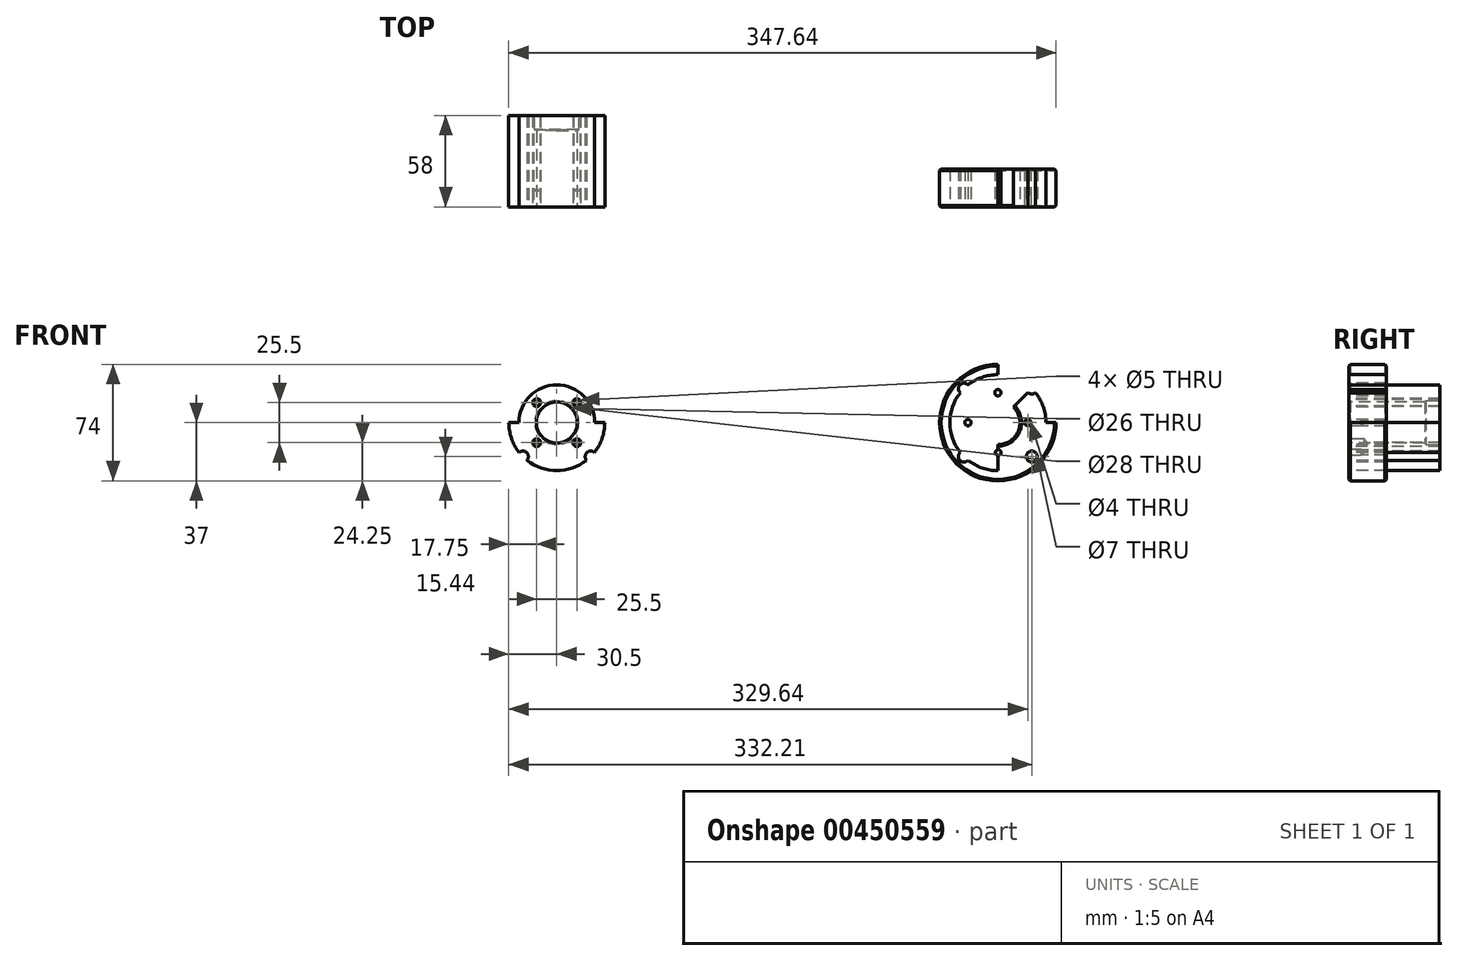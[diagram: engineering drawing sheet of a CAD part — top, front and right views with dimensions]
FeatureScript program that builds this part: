
annotation { "Feature Type Name" : "Feature", "Feature Type Description" : "" }
export const myFeature = defineFeature(function(context is Context, id is Id, definition is map)
    precondition{}
    {
        {
            var Q0;
            Q0=qCreatedBy(makeId("Front.planeOp"),FACE);
            var sketch = newSketch(context, id + "F0", { "sketchPlane" : qUnion([Q0])});
            skLineSegment(sketch, "E0", {"start": v(-17.52, 38.45) * mm, "end": v(-17.52, 26.45) * mm});
            skLineSegment(sketch, "E1", {"start": v(-17.52, -21.55) * mm, "end": v(-17.52, -33.55) * mm});
            skCircle(sketch, "E2", {"center": v(103.48, 2.45) * mm, "radius": 19 * mm});
            skLineSegment(sketch, "E3", {"start": v(103.48, 24.95) * mm, "end": v(103.48, 17.95) * mm});
            skLineSegment(sketch, "E4", {"start": v(103.48, -13.05) * mm, "end": v(103.48, -20.05) * mm});
            skLineSegment(sketch, "E5", {"start": v(-16.52, -34.55) * mm, "end": v(5.48, -34.55) * mm});
            skLineSegment(sketch, "E6", {"start": v(-16.52, 39.45) * mm, "end": v(5.48, 39.45) * mm});
            skLineSegment(sketch, "E7", {"start": v(6.48, -33.55) * mm, "end": v(6.48, -12.55) * mm});
            skLineSegment(sketch, "E8", {"start": v(5.48, -11.55) * mm, "end": v(-26.52, -11.55) * mm});
            skLineSegment(sketch, "E9", {"start": v(-26.52, -10.55) * mm, "end": v(-75.52, -10.55) * mm});
            skLineSegment(sketch, "E10", {"start": v(-74.52, -21.55) * mm, "end": v(-17.52, -21.55) * mm});
            skLineSegment(sketch, "E11", {"start": v(-74.52, 26.45) * mm, "end": v(-17.52, 26.45) * mm});
            skLineSegment(sketch, "E12", {"start": v(-75.52, 25.45) * mm, "end": v(-75.52, -20.55) * mm});
            skLineSegment(sketch, "E13", {"start": v(-5.25, -16.55) * mm, "end": v(6.48, -16.55) * mm});
            skLineSegment(sketch, "E14", {"start": v(6.48, -14.55) * mm, "end": v(-1.52, -14.55) * mm});
            skLineSegment(sketch, "E15", {"start": v(6.48, -18.55) * mm, "end": v(-1.52, -18.55) * mm});
            skLineSegment(sketch, "E16", {"start": v(6.48, -18.17) * mm, "end": v(-4.32, -18.17) * mm});
            skLineSegment(sketch, "E17", {"start": v(6.48, -14.92) * mm, "end": v(-4.32, -14.92) * mm});
            skLineSegment(sketch, "E18", {"start": v(-1.52, -18.55) * mm, "end": v(-1.52, -14.55) * mm});
            skLineSegment(sketch, "E19", {"start": v(-5.25, -16.55) * mm, "end": v(-4.32, -14.92) * mm});
            skLineSegment(sketch, "E20", {"start": v(-4.32, -18.17) * mm, "end": v(-4.32, -14.92) * mm});
            skLineSegment(sketch, "E21", {"start": v(-1.52, -14.55) * mm, "end": v(-2.22, -14.92) * mm});
            skLineSegment(sketch, "E22", {"start": v(-1.52, -18.55) * mm, "end": v(-2.22, -18.17) * mm});
            skLineSegment(sketch, "E23", {"start": v(-5.25, -16.55) * mm, "end": v(-4.32, -18.17) * mm});
            skLineSegment(sketch, "E24", {"start": v(-26.52, -11.55) * mm, "end": v(-26.52, 16.45) * mm});
            skLineSegment(sketch, "E25", {"start": v(5.48, 16.45) * mm, "end": v(-26.52, 16.45) * mm});
            skLineSegment(sketch, "E26", {"start": v(-26.52, 15.45) * mm, "end": v(-75.52, 15.45) * mm});
            skLineSegment(sketch, "E27", {"start": v(125.48, 2.45) * mm, "end": v(119.48, 2.45) * mm});
            skCircle(sketch, "E28", {"center": v(122.48, 2.45) * mm, "radius": 2 * mm});
            skCircle(sketch, "E29", {"center": v(122.48, 2.45) * mm, "radius": 1.62 * mm});
            skLineSegment(sketch, "E30", {"start": v(103.48, 18.45) * mm, "end": v(103.48, 24.45) * mm});
            skCircle(sketch, "E31", {"center": v(103.48, 21.45) * mm, "radius": 2 * mm});
            skCircle(sketch, "E32", {"center": v(103.48, 21.45) * mm, "radius": 1.62 * mm});
            skLineSegment(sketch, "E33", {"start": v(87.48, 2.45) * mm, "end": v(81.48, 2.45) * mm});
            skCircle(sketch, "E34", {"center": v(84.48, 2.45) * mm, "radius": 2 * mm});
            skCircle(sketch, "E35", {"center": v(84.48, 2.45) * mm, "radius": 1.62 * mm});
            skLineSegment(sketch, "E36", {"start": v(103.48, -19.55) * mm, "end": v(103.48, -13.55) * mm});
            skCircle(sketch, "E37", {"center": v(103.48, -16.55) * mm, "radius": 2 * mm});
            skCircle(sketch, "E38", {"center": v(103.48, -16.55) * mm, "radius": 1.62 * mm});
            skCircle(sketch, "E39", {"center": v(103.48, 2.45) * mm, "radius": 14 * mm});
            skLineSegment(sketch, "E40", {"start": v(115.98, 2.45) * mm, "end": v(128.98, 2.45) * mm});
            skCircle(sketch, "E41", {"center": v(103.48, 2.45) * mm, "radius": 13 * mm});
            skCircle(sketch, "E42", {"center": v(-176.66, 2.45) * mm, "radius": 24 * mm});
            skCircle(sketch, "E43", {"center": v(-176.66, 2.45) * mm, "radius": 13 * mm});
            skLineSegment(sketch, "E44", {"start": v(-81.8, 2.45) * mm, "end": v(11.92, 2.45) * mm});
            skLineSegment(sketch, "E45", {"start": v(-163.91, 11.45) * mm, "end": v(-163.91, 18.95) * mm});
            skCircle(sketch, "E46", {"center": v(-163.91, 15.2) * mm, "radius": 2.07 * mm});
            skCircle(sketch, "E47", {"center": v(-163.91, 15.2) * mm, "radius": 2.5 * mm});
            skLineSegment(sketch, "E48", {"start": v(-160.16, 15.2) * mm, "end": v(-167.66, 15.2) * mm});
            skLineSegment(sketch, "E49", {"start": v(-163.91, -14.05) * mm, "end": v(-163.91, -6.55) * mm});
            skCircle(sketch, "E50", {"center": v(-163.91, -10.3) * mm, "radius": 2.07 * mm});
            skCircle(sketch, "E51", {"center": v(-163.91, -10.3) * mm, "radius": 2.5 * mm});
            skLineSegment(sketch, "E52", {"start": v(-160.16, -10.3) * mm, "end": v(-167.66, -10.3) * mm});
            skLineSegment(sketch, "E53", {"start": v(-189.41, -14.05) * mm, "end": v(-189.41, -6.55) * mm});
            skCircle(sketch, "E54", {"center": v(-189.41, -10.3) * mm, "radius": 2.07 * mm});
            skCircle(sketch, "E55", {"center": v(-189.41, -10.3) * mm, "radius": 2.5 * mm});
            skLineSegment(sketch, "E56", {"start": v(-185.66, -10.3) * mm, "end": v(-193.16, -10.3) * mm});
            skLineSegment(sketch, "E57", {"start": v(-189.41, 11.45) * mm, "end": v(-189.41, 18.95) * mm});
            skCircle(sketch, "E58", {"center": v(-189.41, 15.2) * mm, "radius": 2.07 * mm});
            skCircle(sketch, "E59", {"center": v(-189.41, 15.2) * mm, "radius": 2.5 * mm});
            skLineSegment(sketch, "E60", {"start": v(-185.66, 15.2) * mm, "end": v(-193.16, 15.2) * mm});
            skLineSegment(sketch, "E61", {"start": v(103.48, 47.95) * mm, "end": v(103.48, -43.05) * mm});
            skLineSegment(sketch, "E62", {"start": v(57.98, 2.45) * mm, "end": v(148.98, 2.45) * mm});
            skLineSegment(sketch, "E63", {"start": v(-176.66, 47.95) * mm, "end": v(-176.66, -43.05) * mm});
            skLineSegment(sketch, "E64", {"start": v(-222.16, 2.45) * mm, "end": v(-131.16, 2.45) * mm});
            skLineSegment(sketch, "E65", {"start": v(10.78, -9.05) * mm, "end": v(12.23, -11.55) * mm});
            skLineSegment(sketch, "E66", {"start": v(12.23, -11.55) * mm, "end": v(15.4, -6.05) * mm});
            skLineSegment(sketch, "E67", {"start": v(15.4, -6.05) * mm, "end": v(21.78, -6.05) * mm});
            skLineSegment(sketch, "E68", {"start": v(10.78, -9.05) * mm, "end": v(13.67, -9.05) * mm});
            skLineSegment(sketch, "E69", {"start": v(6.48, -33.55) * mm, "end": v(5.48, -34.55) * mm});
            skLineSegment(sketch, "E70", {"start": v(6.48, 38.45) * mm, "end": v(5.48, 39.45) * mm});
            skCircle(sketch, "E71", {"center": v(103.48, 2.45) * mm, "radius": 37 * mm});
            skCircle(sketch, "E72", {"center": v(103.48, 2.45) * mm, "radius": 30.5 * mm});
            skCircle(sketch, "E73", {"center": v(81.92, 24.02) * mm, "radius": 3.5 * mm});
            skCircle(sketch, "E74", {"center": v(81.92, -19.11) * mm, "radius": 3.5 * mm});
            skCircle(sketch, "E75", {"center": v(125.05, 24.02) * mm, "radius": 3.5 * mm});
            skCircle(sketch, "E76", {"center": v(125.05, -19.11) * mm, "radius": 3.5 * mm});
            skCircle(sketch, "E77", {"center": v(-176.66, 2.45) * mm, "radius": 37 * mm});
            skCircle(sketch, "E78", {"center": v(-198.23, 24.02) * mm, "radius": 3.5 * mm});
            skCircle(sketch, "E79", {"center": v(-198.23, -19.11) * mm, "radius": 3.5 * mm});
            skCircle(sketch, "E80", {"center": v(-155.1, 24.02) * mm, "radius": 3.5 * mm});
            skCircle(sketch, "E81", {"center": v(-155.1, -19.11) * mm, "radius": 3.5 * mm});
            skCircle(sketch, "E82", {"center": v(-176.66, 2.45) * mm, "radius": 30.5 * mm});
            skLineSegment(sketch, "E83", {"start": v(128.27, 27.24) * mm, "end": v(121.83, 20.8) * mm});
            skLineSegment(sketch, "E84", {"start": v(78.7, 27.24) * mm, "end": v(85.13, 20.8) * mm});
            skLineSegment(sketch, "E85", {"start": v(78.7, -22.33) * mm, "end": v(85.13, -15.9) * mm});
            skLineSegment(sketch, "E86", {"start": v(128.27, -22.33) * mm, "end": v(121.83, -15.9) * mm});
            skLineSegment(sketch, "E87", {"start": v(-151.88, 27.24) * mm, "end": v(-158.31, 20.8) * mm});
            skLineSegment(sketch, "E88", {"start": v(-201.45, 27.24) * mm, "end": v(-195.01, 20.8) * mm});
            skLineSegment(sketch, "E89", {"start": v(-201.45, -22.33) * mm, "end": v(-195.01, -15.9) * mm});
            skLineSegment(sketch, "E90", {"start": v(-151.88, -22.33) * mm, "end": v(-158.31, -15.9) * mm});
            skLineSegment(sketch, "E91", {"start": v(-24.54, 32.95) * mm, "end": v(11.92, 32.95) * mm});
            skLineSegment(sketch, "E92", {"start": v(-17.52, 36.45) * mm, "end": v(6.48, 36.45) * mm});
            skLineSegment(sketch, "E93", {"start": v(-17.52, 29.45) * mm, "end": v(6.48, 29.45) * mm});
            skLineSegment(sketch, "E94", {"start": v(-61.12, 20.49) * mm, "end": v(-75.52, 20.49) * mm});
            skLineSegment(sketch, "E95", {"start": v(-75.52, 18.42) * mm, "end": v(-62.32, 18.42) * mm});
            skLineSegment(sketch, "E96", {"start": v(-75.52, 22.55) * mm, "end": v(-62.32, 22.55) * mm});
            skLineSegment(sketch, "E97", {"start": v(-62.32, 22.55) * mm, "end": v(-62.32, 18.42) * mm});
            skLineSegment(sketch, "E98", {"start": v(-61.12, 20.49) * mm, "end": v(-62.32, 22.55) * mm});
            skLineSegment(sketch, "E99", {"start": v(-61.12, 20.49) * mm, "end": v(-62.32, 18.42) * mm});
            skLineSegment(sketch, "E100", {"start": v(-75.52, 17.99) * mm, "end": v(-65.52, 17.99) * mm});
            skLineSegment(sketch, "E101", {"start": v(-75.52, 22.99) * mm, "end": v(-65.52, 22.99) * mm});
            skLineSegment(sketch, "E102", {"start": v(-65.52, 22.99) * mm, "end": v(-65.52, 17.99) * mm});
            skLineSegment(sketch, "E103", {"start": v(-65.52, 22.99) * mm, "end": v(-64.72, 22.55) * mm});
            skLineSegment(sketch, "E104", {"start": v(-65.52, 17.99) * mm, "end": v(-64.72, 18.42) * mm});
            skLineSegment(sketch, "E105", {"start": v(103.48, 2.45) * mm, "end": v(134.88, 33.85) * mm});
            skLineSegment(sketch, "E106", {"start": v(103.48, 2.45) * mm, "end": v(103.48, -59.07) * mm});
            skLineSegment(sketch, "E107", {"start": v(135.02, 33.7) * mm, "end": v(136.43, 35.12) * mm});
            skLineSegment(sketch, "E108", {"start": v(134.74, 34) * mm, "end": v(136.15, 35.4) * mm});
            skLineSegment(sketch, "E109", {"start": v(136.43, 35.12) * mm, "end": v(136.15, 35.4) * mm});
            skLineSegment(sketch, "E110", {"start": v(134.74, 34) * mm, "end": v(135.02, 33.7) * mm});
            skLineSegment(sketch, "E111", {"start": v(103.68, -59.07) * mm, "end": v(103.68, -61.07) * mm});
            skLineSegment(sketch, "E112", {"start": v(103.28, -59.07) * mm, "end": v(103.28, -61.07) * mm});
            skLineSegment(sketch, "E113", {"start": v(103.68, -61.07) * mm, "end": v(103.28, -61.07) * mm});
            skLineSegment(sketch, "E114", {"start": v(103.28, -59.07) * mm, "end": v(103.68, -59.07) * mm});
            skLineSegment(sketch, "E115", {"start": v(-16.52, -34.55) * mm, "end": v(-17.52, -33.55) * mm});
            skLineSegment(sketch, "E116", {"start": v(-16.52, 39.45) * mm, "end": v(-17.52, 38.45) * mm});
            skLineSegment(sketch, "E117", {"start": v(-74.52, -21.55) * mm, "end": v(-75.52, -20.55) * mm});
            skLineSegment(sketch, "E118", {"start": v(-74.52, 26.45) * mm, "end": v(-75.52, 25.45) * mm});
            skLineSegment(sketch, "E119", {"start": v(6.48, 17.45) * mm, "end": v(5.48, 16.45) * mm});
            skLineSegment(sketch, "E120", {"start": v(6.48, -12.55) * mm, "end": v(5.48, -11.55) * mm});
            skLineSegment(sketch, "E121", {"start": v(6.48, 38.45) * mm, "end": v(6.48, -12.55) * mm});
            skLineSegment(sketch, "E122", {"start": v(5.48, 16.45) * mm, "end": v(5.48, -11.55) * mm});
            skSolve(sketch);
        }
        {
            var Q0;
            {var subQ3=sQuery(id+"F0.wireOp",EDGE,"E105");var subQ9=makeQuery(id+"F0.imprint","IMPRINT",VERTEX,{"disambiguationData":[OD(1.0)],"derivedFrom":subQ3});Q0=makeQuery(id+"F0.imprint","IMPRINT",FACE,{"disambiguationData":[TD([[makeQuery(id+"F0.imprint","IMPRINT",EDGE,{"disambiguationData":[TD([[subQ9,1.0]])],"derivedFrom":subQ3}),-1.0]])]});}
            var Q1;
            {var subQ0=sQuery(id+"F0.wireOp",EDGE,"E62");var subQ1=makeQuery(id+"F0.imprint","IMPRINT",VERTEX,{"disambiguationData":[OD(4.0)],"derivedFrom":subQ0});Q1=makeQuery(id+"F0.imprint","IMPRINT",FACE,{"disambiguationData":[TD([[makeQuery(id+"F0.imprint","IMPRINT",EDGE,{"disambiguationData":[TD([[subQ1,-1.0]])],"derivedFrom":subQ0}),1.0]])]});}
            var Q2;
            {var subQ0=sQuery(id+"F0.wireOp",EDGE,"E61");var subQ1=makeQuery(id+"F0.imprint","IMPRINT",VERTEX,{"disambiguationData":[OD(0.0)],"derivedFrom":subQ0});Q2=makeQuery(id+"F0.imprint","IMPRINT",FACE,{"disambiguationData":[TD([[makeQuery(id+"F0.imprint","IMPRINT",EDGE,{"disambiguationData":[TD([[subQ1,-1.0]])],"derivedFrom":subQ0}),1.0]])]});}
            var Q3;
            {var subQ3=sQuery(id+"F0.wireOp",EDGE,"E105");var subQ7=makeQuery(id+"F0.imprint","IMPRINT",VERTEX,{"disambiguationData":[OD(1.0)],"derivedFrom":subQ3});Q3=makeQuery(id+"F0.imprint","IMPRINT",FACE,{"disambiguationData":[TD([[makeQuery(id+"F0.imprint","IMPRINT",EDGE,{"disambiguationData":[TD([[subQ7,1.0]])],"derivedFrom":subQ3}),1.0]])]});}
            var Q4;
            {var subQ5=sQuery(id+"F0.wireOp",EDGE,"E71");var subQ6=sQuery(id+"F0.wireOp",EDGE,"E61");var subQ7=makeQuery(id+"F0.imprint","INTERSECT",VERTEX,{"derivedFrom":[subQ6,subQ5]});Q4=makeQuery(id+"F0.imprint","IMPRINT",FACE,{"disambiguationData":[TD([[makeQuery(id+"F0.imprint","IMPRINT",EDGE,{"disambiguationData":[TD([[subQ7,-1.0]])],"derivedFrom":subQ6}),-1.0]])]});}
            var Q5;
            {var subQ1=sQuery(id+"F0.wireOp",EDGE,"E61");var subQ8=makeQuery(id+"F0.imprint","IMPRINT",VERTEX,{"disambiguationData":[OD(0.0)],"derivedFrom":subQ1});Q5=makeQuery(id+"F0.imprint","IMPRINT",FACE,{"disambiguationData":[TD([[makeQuery(id+"F0.imprint","IMPRINT",EDGE,{"disambiguationData":[TD([[subQ8,-1.0]])],"derivedFrom":subQ1}),-1.0]])]});}
            var Q6;
            {var subQ3=sQuery(id+"F0.wireOp",EDGE,"E61");var subQ12=makeQuery(id+"F0.imprint","IMPRINT",VERTEX,{"disambiguationData":[OD(2.0)],"derivedFrom":subQ3});Q6=makeQuery(id+"F0.imprint","IMPRINT",FACE,{"disambiguationData":[TD([[makeQuery(id+"F0.imprint","IMPRINT",EDGE,{"disambiguationData":[TD([[subQ12,-1.0]])],"derivedFrom":subQ3}),-1.0]])]});}
            var Q7;
            {var subQ0=sQuery(id+"F0.wireOp",EDGE,"E61");var subQ1=makeQuery(id+"F0.imprint","IMPRINT",VERTEX,{"disambiguationData":[OD(2.0)],"derivedFrom":subQ0});Q7=makeQuery(id+"F0.imprint","IMPRINT",FACE,{"disambiguationData":[TD([[makeQuery(id+"F0.imprint","IMPRINT",EDGE,{"disambiguationData":[TD([[subQ1,-1.0]])],"derivedFrom":subQ0}),1.0]])]});}
            var Q8;
            {var subQ0=sQuery(id+"F0.wireOp",EDGE,"E84");var subQ1=sQuery(id+"F0.wireOp",EDGE,"E72");var subQ2=makeQuery(id+"F0.imprint","INTERSECT",VERTEX,{"derivedFrom":[subQ1,subQ0]});Q8=makeQuery(id+"F0.imprint","IMPRINT",FACE,{"disambiguationData":[TD([[makeQuery(id+"F0.imprint","IMPRINT",EDGE,{"disambiguationData":[TD([[subQ2,-1.0]])],"derivedFrom":subQ1}),1.0]])]});}
            var Q9;
            {var subQ0=sQuery(id+"F0.wireOp",EDGE,"E73");var subQ1=sQuery(id+"F0.wireOp",EDGE,"E72");var subQ2=makeQuery(id+"F0.imprint","INTERSECT",VERTEX,{"disambiguationData":[OD(0.0)],"derivedFrom":[subQ1,subQ0]});Q9=makeQuery(id+"F0.imprint","IMPRINT",FACE,{"disambiguationData":[TD([[makeQuery(id+"F0.imprint","IMPRINT",EDGE,{"disambiguationData":[TD([[subQ2,-1.0]])],"derivedFrom":subQ1}),1.0]])]});}
            var Q10;
            {var subQ0=sQuery(id+"F0.wireOp",EDGE,"E73");var subQ1=sQuery(id+"F0.wireOp",EDGE,"E72");var subQ2=makeQuery(id+"F0.imprint","INTERSECT",VERTEX,{"disambiguationData":[OD(0.0)],"derivedFrom":[subQ1,subQ0]});Q10=makeQuery(id+"F0.imprint","IMPRINT",FACE,{"disambiguationData":[TD([[makeQuery(id+"F0.imprint","IMPRINT",EDGE,{"disambiguationData":[TD([[subQ2,-1.0]])],"derivedFrom":subQ1}),-1.0]])]});}
            var Q11;
            {var subQ0=sQuery(id+"F0.wireOp",EDGE,"E84");var subQ1=sQuery(id+"F0.wireOp",EDGE,"E72");var subQ2=makeQuery(id+"F0.imprint","INTERSECT",VERTEX,{"derivedFrom":[subQ1,subQ0]});Q11=makeQuery(id+"F0.imprint","IMPRINT",FACE,{"disambiguationData":[TD([[makeQuery(id+"F0.imprint","IMPRINT",EDGE,{"disambiguationData":[TD([[subQ2,-1.0]])],"derivedFrom":subQ1}),-1.0]])]});}
            var Q12;
            {var subQ0=sQuery(id+"F0.wireOp",EDGE,"E75");var subQ1=sQuery(id+"F0.wireOp",EDGE,"E72");var subQ2=makeQuery(id+"F0.imprint","INTERSECT",VERTEX,{"disambiguationData":[OD(0.0)],"derivedFrom":[subQ1,subQ0]});Q12=makeQuery(id+"F0.imprint","IMPRINT",FACE,{"disambiguationData":[TD([[makeQuery(id+"F0.imprint","IMPRINT",EDGE,{"disambiguationData":[TD([[subQ2,-1.0]])],"derivedFrom":subQ1}),1.0]])]});}
            var Q13;
            {var subQ0=sQuery(id+"F0.wireOp",EDGE,"E105");var subQ1=sQuery(id+"F0.wireOp",EDGE,"E72");var subQ2=makeQuery(id+"F0.imprint","INTERSECT",VERTEX,{"derivedFrom":[subQ1,subQ0]});Q13=makeQuery(id+"F0.imprint","IMPRINT",FACE,{"disambiguationData":[TD([[makeQuery(id+"F0.imprint","IMPRINT",EDGE,{"disambiguationData":[TD([[subQ2,-1.0]])],"derivedFrom":subQ1}),1.0]])]});}
            var Q14;
            {var subQ0=sQuery(id+"F0.wireOp",EDGE,"E75");var subQ1=sQuery(id+"F0.wireOp",EDGE,"E72");var subQ2=makeQuery(id+"F0.imprint","INTERSECT",VERTEX,{"disambiguationData":[OD(0.0)],"derivedFrom":[subQ1,subQ0]});Q14=makeQuery(id+"F0.imprint","IMPRINT",FACE,{"disambiguationData":[TD([[makeQuery(id+"F0.imprint","IMPRINT",EDGE,{"disambiguationData":[TD([[subQ2,-1.0]])],"derivedFrom":subQ1}),-1.0]])]});}
            var Q15;
            {var subQ0=sQuery(id+"F0.wireOp",EDGE,"E105");var subQ1=sQuery(id+"F0.wireOp",EDGE,"E72");var subQ2=makeQuery(id+"F0.imprint","INTERSECT",VERTEX,{"derivedFrom":[subQ1,subQ0]});Q15=makeQuery(id+"F0.imprint","IMPRINT",FACE,{"disambiguationData":[TD([[makeQuery(id+"F0.imprint","IMPRINT",EDGE,{"disambiguationData":[TD([[subQ2,-1.0]])],"derivedFrom":subQ1}),-1.0]])]});}
            var Q16;
            {var subQ0=sQuery(id+"F0.wireOp",EDGE,"E76");var subQ1=sQuery(id+"F0.wireOp",EDGE,"E72");var subQ2=makeQuery(id+"F0.imprint","INTERSECT",VERTEX,{"disambiguationData":[OD(0.0)],"derivedFrom":[subQ1,subQ0]});Q16=makeQuery(id+"F0.imprint","IMPRINT",FACE,{"disambiguationData":[TD([[makeQuery(id+"F0.imprint","IMPRINT",EDGE,{"disambiguationData":[TD([[subQ2,-1.0]])],"derivedFrom":subQ1}),1.0]])]});}
            var Q17;
            {var subQ0=sQuery(id+"F0.wireOp",EDGE,"E86");var subQ1=sQuery(id+"F0.wireOp",EDGE,"E72");var subQ2=makeQuery(id+"F0.imprint","INTERSECT",VERTEX,{"derivedFrom":[subQ1,subQ0]});Q17=makeQuery(id+"F0.imprint","IMPRINT",FACE,{"disambiguationData":[TD([[makeQuery(id+"F0.imprint","IMPRINT",EDGE,{"disambiguationData":[TD([[subQ2,-1.0]])],"derivedFrom":subQ1}),1.0]])]});}
            var Q18;
            {var subQ0=sQuery(id+"F0.wireOp",EDGE,"E76");var subQ1=sQuery(id+"F0.wireOp",EDGE,"E72");var subQ2=makeQuery(id+"F0.imprint","INTERSECT",VERTEX,{"disambiguationData":[OD(0.0)],"derivedFrom":[subQ1,subQ0]});Q18=makeQuery(id+"F0.imprint","IMPRINT",FACE,{"disambiguationData":[TD([[makeQuery(id+"F0.imprint","IMPRINT",EDGE,{"disambiguationData":[TD([[subQ2,-1.0]])],"derivedFrom":subQ1}),-1.0]])]});}
            var Q19;
            {var subQ4=sQuery(id+"F0.wireOp",EDGE,"E62");var subQ7=makeQuery(id+"F0.imprint","IMPRINT",VERTEX,{"disambiguationData":[OD(4.0)],"derivedFrom":subQ4});Q19=makeQuery(id+"F0.imprint","IMPRINT",FACE,{"disambiguationData":[TD([[makeQuery(id+"F0.imprint","IMPRINT",EDGE,{"disambiguationData":[TD([[subQ7,-1.0]])],"derivedFrom":subQ4}),-1.0]])]});}
            var Q20;
            {var subQ1=sQuery(id+"F0.wireOp",EDGE,"E62");var subQ5=sQuery(id+"F0.wireOp",EDGE,"E71");var subQ6=makeQuery(id+"F0.imprint","INTERSECT",VERTEX,{"disambiguationData":[OD(1.0)],"derivedFrom":[subQ1,subQ5]});Q20=makeQuery(id+"F0.imprint","IMPRINT",FACE,{"disambiguationData":[TD([[makeQuery(id+"F0.imprint","IMPRINT",EDGE,{"disambiguationData":[TD([[subQ6,1.0]])],"derivedFrom":subQ1}),-1.0]])]});}
            var Q21;
            {var subQ0=sQuery(id+"F0.wireOp",EDGE,"E86");var subQ1=sQuery(id+"F0.wireOp",EDGE,"E72");var subQ2=makeQuery(id+"F0.imprint","INTERSECT",VERTEX,{"derivedFrom":[subQ1,subQ0]});Q21=makeQuery(id+"F0.imprint","IMPRINT",FACE,{"disambiguationData":[TD([[makeQuery(id+"F0.imprint","IMPRINT",EDGE,{"disambiguationData":[TD([[subQ2,-1.0]])],"derivedFrom":subQ1}),-1.0]])]});}
            var Q22;
            {var subQ0=sQuery(id+"F0.wireOp",EDGE,"E106");var subQ13=makeQuery(id+"F0.imprint","IMPRINT",VERTEX,{"disambiguationData":[OD(0.0)],"derivedFrom":subQ0});Q22=makeQuery(id+"F0.imprint","IMPRINT",FACE,{"disambiguationData":[TD([[makeQuery(id+"F0.imprint","IMPRINT",EDGE,{"disambiguationData":[TD([[subQ13,-1.0]])],"derivedFrom":subQ0}),1.0]])]});}
            var Q23;
            {var subQ0=sQuery(id+"F0.wireOp",EDGE,"E62");var subQ9=makeQuery(id+"F0.imprint","IMPRINT",VERTEX,{"disambiguationData":[OD(3.0)],"derivedFrom":subQ0});Q23=makeQuery(id+"F0.imprint","IMPRINT",FACE,{"disambiguationData":[TD([[makeQuery(id+"F0.imprint","IMPRINT",EDGE,{"disambiguationData":[TD([[subQ9,1.0]])],"derivedFrom":subQ0}),1.0]])]});}
            var Q24;
            {var subQ3=sQuery(id+"F0.wireOp",EDGE,"E106");var subQ13=makeQuery(id+"F0.imprint","IMPRINT",VERTEX,{"disambiguationData":[OD(0.0)],"derivedFrom":subQ3});Q24=makeQuery(id+"F0.imprint","IMPRINT",FACE,{"disambiguationData":[TD([[makeQuery(id+"F0.imprint","IMPRINT",EDGE,{"disambiguationData":[TD([[subQ13,-1.0]])],"derivedFrom":subQ3}),-1.0]])]});}
            var Q25;
            {var subQ0=sQuery(id+"F0.wireOp",EDGE,"E106");var subQ1=makeQuery(id+"F0.imprint","IMPRINT",VERTEX,{"disambiguationData":[OD(2.0)],"derivedFrom":subQ0});Q25=makeQuery(id+"F0.imprint","IMPRINT",FACE,{"disambiguationData":[TD([[makeQuery(id+"F0.imprint","IMPRINT",EDGE,{"disambiguationData":[TD([[subQ1,-1.0]])],"derivedFrom":subQ0}),-1.0]])]});}
            var Q26;
            {var subQ0=sQuery(id+"F0.wireOp",EDGE,"E85");var subQ1=sQuery(id+"F0.wireOp",EDGE,"E72");var subQ2=makeQuery(id+"F0.imprint","INTERSECT",VERTEX,{"derivedFrom":[subQ1,subQ0]});Q26=makeQuery(id+"F0.imprint","IMPRINT",FACE,{"disambiguationData":[TD([[makeQuery(id+"F0.imprint","IMPRINT",EDGE,{"disambiguationData":[TD([[subQ2,-1.0]])],"derivedFrom":subQ1}),-1.0]])]});}
            var Q27;
            {var subQ0=sQuery(id+"F0.wireOp",EDGE,"E85");var subQ1=sQuery(id+"F0.wireOp",EDGE,"E72");var subQ2=makeQuery(id+"F0.imprint","INTERSECT",VERTEX,{"derivedFrom":[subQ1,subQ0]});Q27=makeQuery(id+"F0.imprint","IMPRINT",FACE,{"disambiguationData":[TD([[makeQuery(id+"F0.imprint","IMPRINT",EDGE,{"disambiguationData":[TD([[subQ2,-1.0]])],"derivedFrom":subQ1}),1.0]])]});}
            var Q28;
            {var subQ0=sQuery(id+"F0.wireOp",EDGE,"E74");var subQ1=sQuery(id+"F0.wireOp",EDGE,"E72");var subQ2=makeQuery(id+"F0.imprint","INTERSECT",VERTEX,{"disambiguationData":[OD(0.0)],"derivedFrom":[subQ1,subQ0]});Q28=makeQuery(id+"F0.imprint","IMPRINT",FACE,{"disambiguationData":[TD([[makeQuery(id+"F0.imprint","IMPRINT",EDGE,{"disambiguationData":[TD([[subQ2,-1.0]])],"derivedFrom":subQ1}),-1.0]])]});}
            var Q29;
            {var subQ0=sQuery(id+"F0.wireOp",EDGE,"E74");var subQ1=sQuery(id+"F0.wireOp",EDGE,"E72");var subQ2=makeQuery(id+"F0.imprint","INTERSECT",VERTEX,{"disambiguationData":[OD(0.0)],"derivedFrom":[subQ1,subQ0]});Q29=makeQuery(id+"F0.imprint","IMPRINT",FACE,{"disambiguationData":[TD([[makeQuery(id+"F0.imprint","IMPRINT",EDGE,{"disambiguationData":[TD([[subQ2,-1.0]])],"derivedFrom":subQ1}),1.0]])]});}
            var Q30;
            {var subQ1=sQuery(id+"F0.wireOp",EDGE,"E62");var subQ5=sQuery(id+"F0.wireOp",EDGE,"E71");var subQ6=makeQuery(id+"F0.imprint","INTERSECT",VERTEX,{"disambiguationData":[OD(0.0)],"derivedFrom":[subQ1,subQ5]});Q30=makeQuery(id+"F0.imprint","IMPRINT",FACE,{"disambiguationData":[TD([[makeQuery(id+"F0.imprint","IMPRINT",EDGE,{"disambiguationData":[TD([[subQ6,-1.0]])],"derivedFrom":subQ1}),-1.0]])]});}
            var Q31;
            {var subQ0=sQuery(id+"F0.wireOp",EDGE,"E28");var subQ1=sQuery(id+"F0.wireOp",EDGE,"E2");var subQ2=makeQuery(id+"F0.imprint","INTERSECT",VERTEX,{"disambiguationData":[OD(1.0)],"derivedFrom":[subQ1,subQ0]});Q31=makeQuery(id+"F0.imprint","IMPRINT",FACE,{"disambiguationData":[TD([[makeQuery(id+"F0.imprint","IMPRINT",EDGE,{"disambiguationData":[TD([[subQ2,-1.0]])],"derivedFrom":subQ1}),-1.0]])]});}
            var Q32;
            {var subQ0=sQuery(id+"F0.wireOp",EDGE,"E29");var subQ1=sQuery(id+"F0.wireOp",EDGE,"E2");var subQ2=makeQuery(id+"F0.imprint","INTERSECT",VERTEX,{"disambiguationData":[OD(0.0)],"derivedFrom":[subQ1,subQ0]});Q32=makeQuery(id+"F0.imprint","IMPRINT",FACE,{"disambiguationData":[TD([[makeQuery(id+"F0.imprint","IMPRINT",EDGE,{"disambiguationData":[TD([[subQ2,1.0]])],"derivedFrom":subQ1}),-1.0]])]});}
            var Q33;
            {var subQ0=sQuery(id+"F0.wireOp",EDGE,"E29");var subQ1=sQuery(id+"F0.wireOp",EDGE,"E2");var subQ2=makeQuery(id+"F0.imprint","INTERSECT",VERTEX,{"disambiguationData":[OD(0.0)],"derivedFrom":[subQ1,subQ0]});Q33=makeQuery(id+"F0.imprint","IMPRINT",FACE,{"disambiguationData":[TD([[makeQuery(id+"F0.imprint","IMPRINT",EDGE,{"disambiguationData":[TD([[subQ2,1.0]])],"derivedFrom":subQ1}),1.0]])]});}
            var Q34;
            {var subQ0=sQuery(id+"F0.wireOp",EDGE,"E29");var subQ1=sQuery(id+"F0.wireOp",EDGE,"E2");var subQ2=makeQuery(id+"F0.imprint","INTERSECT",VERTEX,{"disambiguationData":[OD(0.0)],"derivedFrom":[subQ1,subQ0]});Q34=makeQuery(id+"F0.imprint","IMPRINT",FACE,{"disambiguationData":[TD([[makeQuery(id+"F0.imprint","IMPRINT",EDGE,{"disambiguationData":[TD([[subQ2,-1.0]])],"derivedFrom":subQ1}),-1.0]])]});}
            var Q35;
            {var subQ0=sQuery(id+"F0.wireOp",EDGE,"E62");var subQ1=sQuery(id+"F0.wireOp",EDGE,"E2");var subQ2=makeQuery(id+"F0.imprint","INTERSECT",VERTEX,{"disambiguationData":[OD(0.0)],"derivedFrom":[subQ1,subQ0]});Q35=makeQuery(id+"F0.imprint","IMPRINT",FACE,{"disambiguationData":[TD([[makeQuery(id+"F0.imprint","IMPRINT",EDGE,{"disambiguationData":[TD([[subQ2,1.0]])],"derivedFrom":subQ1}),-1.0]])]});}
            var Q36;
            {var subQ0=sQuery(id+"F0.wireOp",EDGE,"E29");var subQ1=sQuery(id+"F0.wireOp",EDGE,"E2");var subQ2=makeQuery(id+"F0.imprint","INTERSECT",VERTEX,{"disambiguationData":[OD(0.0)],"derivedFrom":[subQ1,subQ0]});Q36=makeQuery(id+"F0.imprint","IMPRINT",FACE,{"disambiguationData":[TD([[makeQuery(id+"F0.imprint","IMPRINT",EDGE,{"disambiguationData":[TD([[subQ2,-1.0]])],"derivedFrom":subQ1}),1.0]])]});}
            var Q37;
            {var subQ0=sQuery(id+"F0.wireOp",EDGE,"E62");var subQ1=sQuery(id+"F0.wireOp",EDGE,"E2");var subQ2=makeQuery(id+"F0.imprint","INTERSECT",VERTEX,{"disambiguationData":[OD(0.0)],"derivedFrom":[subQ1,subQ0]});Q37=makeQuery(id+"F0.imprint","IMPRINT",FACE,{"disambiguationData":[TD([[makeQuery(id+"F0.imprint","IMPRINT",EDGE,{"disambiguationData":[TD([[subQ2,1.0]])],"derivedFrom":subQ1}),1.0]])]});}
            var Q38;
            {var subQ0=sQuery(id+"F0.wireOp",EDGE,"E28");var subQ1=sQuery(id+"F0.wireOp",EDGE,"E2");var subQ2=makeQuery(id+"F0.imprint","INTERSECT",VERTEX,{"disambiguationData":[OD(1.0)],"derivedFrom":[subQ1,subQ0]});Q38=makeQuery(id+"F0.imprint","IMPRINT",FACE,{"disambiguationData":[TD([[makeQuery(id+"F0.imprint","IMPRINT",EDGE,{"disambiguationData":[TD([[subQ2,-1.0]])],"derivedFrom":subQ1}),1.0]])]});}
            var Q39;
            {var subQ0=sQuery(id+"F0.wireOp",EDGE,"E32");var subQ1=sQuery(id+"F0.wireOp",EDGE,"E2");var subQ2=makeQuery(id+"F0.imprint","INTERSECT",VERTEX,{"disambiguationData":[OD(0.0)],"derivedFrom":[subQ1,subQ0]});Q39=makeQuery(id+"F0.imprint","IMPRINT",FACE,{"disambiguationData":[TD([[makeQuery(id+"F0.imprint","IMPRINT",EDGE,{"disambiguationData":[TD([[subQ2,-1.0]])],"derivedFrom":subQ1}),1.0]])]});}
            var Q40;
            {var subQ0=sQuery(id+"F0.wireOp",EDGE,"E32");var subQ1=sQuery(id+"F0.wireOp",EDGE,"E2");var subQ2=makeQuery(id+"F0.imprint","INTERSECT",VERTEX,{"disambiguationData":[OD(1.0)],"derivedFrom":[subQ1,subQ0]});Q40=makeQuery(id+"F0.imprint","IMPRINT",FACE,{"disambiguationData":[TD([[makeQuery(id+"F0.imprint","IMPRINT",EDGE,{"disambiguationData":[TD([[subQ2,-1.0]])],"derivedFrom":subQ1}),1.0]])]});}
            var Q41;
            {var subQ0=sQuery(id+"F0.wireOp",EDGE,"E32");var subQ1=sQuery(id+"F0.wireOp",EDGE,"E2");var subQ2=makeQuery(id+"F0.imprint","INTERSECT",VERTEX,{"disambiguationData":[OD(0.0)],"derivedFrom":[subQ1,subQ0]});Q41=makeQuery(id+"F0.imprint","IMPRINT",FACE,{"disambiguationData":[TD([[makeQuery(id+"F0.imprint","IMPRINT",EDGE,{"disambiguationData":[TD([[subQ2,-1.0]])],"derivedFrom":subQ1}),-1.0]])]});}
            var Q42;
            {var subQ0=sQuery(id+"F0.wireOp",EDGE,"E31");var subQ1=sQuery(id+"F0.wireOp",EDGE,"E2");var subQ2=makeQuery(id+"F0.imprint","INTERSECT",VERTEX,{"disambiguationData":[OD(0.0)],"derivedFrom":[subQ1,subQ0]});Q42=makeQuery(id+"F0.imprint","IMPRINT",FACE,{"disambiguationData":[TD([[makeQuery(id+"F0.imprint","IMPRINT",EDGE,{"disambiguationData":[TD([[subQ2,-1.0]])],"derivedFrom":subQ1}),1.0]])]});}
            var Q43;
            {var subQ0=sQuery(id+"F0.wireOp",EDGE,"E31");var subQ1=sQuery(id+"F0.wireOp",EDGE,"E2");var subQ2=makeQuery(id+"F0.imprint","INTERSECT",VERTEX,{"disambiguationData":[OD(0.0)],"derivedFrom":[subQ1,subQ0]});Q43=makeQuery(id+"F0.imprint","IMPRINT",FACE,{"disambiguationData":[TD([[makeQuery(id+"F0.imprint","IMPRINT",EDGE,{"disambiguationData":[TD([[subQ2,-1.0]])],"derivedFrom":subQ1}),-1.0]])]});}
            var Q44;
            {var subQ0=sQuery(id+"F0.wireOp",EDGE,"E32");var subQ1=sQuery(id+"F0.wireOp",EDGE,"E2");var subQ2=makeQuery(id+"F0.imprint","INTERSECT",VERTEX,{"disambiguationData":[OD(1.0)],"derivedFrom":[subQ1,subQ0]});Q44=makeQuery(id+"F0.imprint","IMPRINT",FACE,{"disambiguationData":[TD([[makeQuery(id+"F0.imprint","IMPRINT",EDGE,{"disambiguationData":[TD([[subQ2,-1.0]])],"derivedFrom":subQ1}),-1.0]])]});}
            var Q45;
            {var subQ0=sQuery(id+"F0.wireOp",EDGE,"E61");var subQ1=sQuery(id+"F0.wireOp",EDGE,"E2");var subQ2=makeQuery(id+"F0.imprint","INTERSECT",VERTEX,{"derivedFrom":[subQ1,subQ0]});Q45=makeQuery(id+"F0.imprint","IMPRINT",FACE,{"disambiguationData":[TD([[makeQuery(id+"F0.imprint","IMPRINT",EDGE,{"disambiguationData":[TD([[subQ2,-1.0]])],"derivedFrom":subQ1}),1.0]])]});}
            var Q46;
            {var subQ0=sQuery(id+"F0.wireOp",EDGE,"E61");var subQ1=sQuery(id+"F0.wireOp",EDGE,"E2");var subQ2=makeQuery(id+"F0.imprint","INTERSECT",VERTEX,{"derivedFrom":[subQ1,subQ0]});Q46=makeQuery(id+"F0.imprint","IMPRINT",FACE,{"disambiguationData":[TD([[makeQuery(id+"F0.imprint","IMPRINT",EDGE,{"disambiguationData":[TD([[subQ2,-1.0]])],"derivedFrom":subQ1}),-1.0]])]});}
            var Q47;
            {var subQ0=sQuery(id+"F0.wireOp",EDGE,"E35");var subQ1=sQuery(id+"F0.wireOp",EDGE,"E2");var subQ2=makeQuery(id+"F0.imprint","INTERSECT",VERTEX,{"disambiguationData":[OD(1.0)],"derivedFrom":[subQ1,subQ0]});Q47=makeQuery(id+"F0.imprint","IMPRINT",FACE,{"disambiguationData":[TD([[makeQuery(id+"F0.imprint","IMPRINT",EDGE,{"disambiguationData":[TD([[subQ2,-1.0]])],"derivedFrom":subQ1}),-1.0]])]});}
            var Q48;
            {var subQ0=sQuery(id+"F0.wireOp",EDGE,"E35");var subQ1=sQuery(id+"F0.wireOp",EDGE,"E2");var subQ2=makeQuery(id+"F0.imprint","INTERSECT",VERTEX,{"disambiguationData":[OD(1.0)],"derivedFrom":[subQ1,subQ0]});Q48=makeQuery(id+"F0.imprint","IMPRINT",FACE,{"disambiguationData":[TD([[makeQuery(id+"F0.imprint","IMPRINT",EDGE,{"disambiguationData":[TD([[subQ2,-1.0]])],"derivedFrom":subQ1}),1.0]])]});}
            var Q49;
            {var subQ0=sQuery(id+"F0.wireOp",EDGE,"E34");var subQ1=sQuery(id+"F0.wireOp",EDGE,"E2");var subQ2=makeQuery(id+"F0.imprint","INTERSECT",VERTEX,{"disambiguationData":[OD(0.0)],"derivedFrom":[subQ1,subQ0]});Q49=makeQuery(id+"F0.imprint","IMPRINT",FACE,{"disambiguationData":[TD([[makeQuery(id+"F0.imprint","IMPRINT",EDGE,{"disambiguationData":[TD([[subQ2,-1.0]])],"derivedFrom":subQ1}),-1.0]])]});}
            var Q50;
            {var subQ0=sQuery(id+"F0.wireOp",EDGE,"E35");var subQ1=sQuery(id+"F0.wireOp",EDGE,"E2");var subQ2=makeQuery(id+"F0.imprint","INTERSECT",VERTEX,{"disambiguationData":[OD(0.0)],"derivedFrom":[subQ1,subQ0]});Q50=makeQuery(id+"F0.imprint","IMPRINT",FACE,{"disambiguationData":[TD([[makeQuery(id+"F0.imprint","IMPRINT",EDGE,{"disambiguationData":[TD([[subQ2,-1.0]])],"derivedFrom":subQ1}),-1.0]])]});}
            var Q51;
            {var subQ0=sQuery(id+"F0.wireOp",EDGE,"E62");var subQ1=sQuery(id+"F0.wireOp",EDGE,"E2");var subQ2=makeQuery(id+"F0.imprint","INTERSECT",VERTEX,{"disambiguationData":[OD(1.0)],"derivedFrom":[subQ1,subQ0]});Q51=makeQuery(id+"F0.imprint","IMPRINT",FACE,{"disambiguationData":[TD([[makeQuery(id+"F0.imprint","IMPRINT",EDGE,{"disambiguationData":[TD([[subQ2,-1.0]])],"derivedFrom":subQ1}),1.0]])]});}
            var Q52;
            {var subQ0=sQuery(id+"F0.wireOp",EDGE,"E35");var subQ1=sQuery(id+"F0.wireOp",EDGE,"E2");var subQ2=makeQuery(id+"F0.imprint","INTERSECT",VERTEX,{"disambiguationData":[OD(0.0)],"derivedFrom":[subQ1,subQ0]});Q52=makeQuery(id+"F0.imprint","IMPRINT",FACE,{"disambiguationData":[TD([[makeQuery(id+"F0.imprint","IMPRINT",EDGE,{"disambiguationData":[TD([[subQ2,-1.0]])],"derivedFrom":subQ1}),1.0]])]});}
            var Q53;
            {var subQ0=sQuery(id+"F0.wireOp",EDGE,"E34");var subQ1=sQuery(id+"F0.wireOp",EDGE,"E2");var subQ2=makeQuery(id+"F0.imprint","INTERSECT",VERTEX,{"disambiguationData":[OD(0.0)],"derivedFrom":[subQ1,subQ0]});Q53=makeQuery(id+"F0.imprint","IMPRINT",FACE,{"disambiguationData":[TD([[makeQuery(id+"F0.imprint","IMPRINT",EDGE,{"disambiguationData":[TD([[subQ2,-1.0]])],"derivedFrom":subQ1}),1.0]])]});}
            var Q54;
            {var subQ0=sQuery(id+"F0.wireOp",EDGE,"E62");var subQ1=sQuery(id+"F0.wireOp",EDGE,"E2");var subQ2=makeQuery(id+"F0.imprint","INTERSECT",VERTEX,{"disambiguationData":[OD(1.0)],"derivedFrom":[subQ1,subQ0]});Q54=makeQuery(id+"F0.imprint","IMPRINT",FACE,{"disambiguationData":[TD([[makeQuery(id+"F0.imprint","IMPRINT",EDGE,{"disambiguationData":[TD([[subQ2,-1.0]])],"derivedFrom":subQ1}),-1.0]])]});}
            var Q55;
            {var subQ0=sQuery(id+"F0.wireOp",EDGE,"E38");var subQ1=sQuery(id+"F0.wireOp",EDGE,"E2");var subQ2=makeQuery(id+"F0.imprint","INTERSECT",VERTEX,{"disambiguationData":[OD(1.0)],"derivedFrom":[subQ1,subQ0]});Q55=makeQuery(id+"F0.imprint","IMPRINT",FACE,{"disambiguationData":[TD([[makeQuery(id+"F0.imprint","IMPRINT",EDGE,{"disambiguationData":[TD([[subQ2,-1.0]])],"derivedFrom":subQ1}),-1.0]])]});}
            var Q56;
            {var subQ0=sQuery(id+"F0.wireOp",EDGE,"E38");var subQ1=sQuery(id+"F0.wireOp",EDGE,"E2");var subQ2=makeQuery(id+"F0.imprint","INTERSECT",VERTEX,{"disambiguationData":[OD(1.0)],"derivedFrom":[subQ1,subQ0]});Q56=makeQuery(id+"F0.imprint","IMPRINT",FACE,{"disambiguationData":[TD([[makeQuery(id+"F0.imprint","IMPRINT",EDGE,{"disambiguationData":[TD([[subQ2,-1.0]])],"derivedFrom":subQ1}),1.0]])]});}
            var Q57;
            {var subQ0=sQuery(id+"F0.wireOp",EDGE,"E106");var subQ1=sQuery(id+"F0.wireOp",EDGE,"E2");var subQ2=makeQuery(id+"F0.imprint","INTERSECT",VERTEX,{"derivedFrom":[subQ1,subQ0]});Q57=makeQuery(id+"F0.imprint","IMPRINT",FACE,{"disambiguationData":[TD([[makeQuery(id+"F0.imprint","IMPRINT",EDGE,{"disambiguationData":[TD([[subQ2,-1.0]])],"derivedFrom":subQ1}),1.0]])]});}
            var Q58;
            {var subQ0=sQuery(id+"F0.wireOp",EDGE,"E38");var subQ1=sQuery(id+"F0.wireOp",EDGE,"E2");var subQ2=makeQuery(id+"F0.imprint","INTERSECT",VERTEX,{"disambiguationData":[OD(0.0)],"derivedFrom":[subQ1,subQ0]});Q58=makeQuery(id+"F0.imprint","IMPRINT",FACE,{"disambiguationData":[TD([[makeQuery(id+"F0.imprint","IMPRINT",EDGE,{"disambiguationData":[TD([[subQ2,-1.0]])],"derivedFrom":subQ1}),1.0]])]});}
            var Q59;
            {var subQ0=sQuery(id+"F0.wireOp",EDGE,"E106");var subQ1=sQuery(id+"F0.wireOp",EDGE,"E2");var subQ2=makeQuery(id+"F0.imprint","INTERSECT",VERTEX,{"derivedFrom":[subQ1,subQ0]});Q59=makeQuery(id+"F0.imprint","IMPRINT",FACE,{"disambiguationData":[TD([[makeQuery(id+"F0.imprint","IMPRINT",EDGE,{"disambiguationData":[TD([[subQ2,-1.0]])],"derivedFrom":subQ1}),-1.0]])]});}
            var Q60;
            {var subQ0=sQuery(id+"F0.wireOp",EDGE,"E38");var subQ1=sQuery(id+"F0.wireOp",EDGE,"E2");var subQ2=makeQuery(id+"F0.imprint","INTERSECT",VERTEX,{"disambiguationData":[OD(0.0)],"derivedFrom":[subQ1,subQ0]});Q60=makeQuery(id+"F0.imprint","IMPRINT",FACE,{"disambiguationData":[TD([[makeQuery(id+"F0.imprint","IMPRINT",EDGE,{"disambiguationData":[TD([[subQ2,-1.0]])],"derivedFrom":subQ1}),-1.0]])]});}
            var Q61;
            {var subQ0=sQuery(id+"F0.wireOp",EDGE,"E37");var subQ1=sQuery(id+"F0.wireOp",EDGE,"E2");var subQ2=makeQuery(id+"F0.imprint","INTERSECT",VERTEX,{"disambiguationData":[OD(0.0)],"derivedFrom":[subQ1,subQ0]});Q61=makeQuery(id+"F0.imprint","IMPRINT",FACE,{"disambiguationData":[TD([[makeQuery(id+"F0.imprint","IMPRINT",EDGE,{"disambiguationData":[TD([[subQ2,-1.0]])],"derivedFrom":subQ1}),1.0]])]});}
            var Q62;
            {var subQ0=sQuery(id+"F0.wireOp",EDGE,"E37");var subQ1=sQuery(id+"F0.wireOp",EDGE,"E2");var subQ2=makeQuery(id+"F0.imprint","INTERSECT",VERTEX,{"disambiguationData":[OD(0.0)],"derivedFrom":[subQ1,subQ0]});Q62=makeQuery(id+"F0.imprint","IMPRINT",FACE,{"disambiguationData":[TD([[makeQuery(id+"F0.imprint","IMPRINT",EDGE,{"disambiguationData":[TD([[subQ2,-1.0]])],"derivedFrom":subQ1}),-1.0]])]});}
            extrude(context, id + "F1", {"entities" : qUnion([Q0, Q1, Q2, Q3, Q4, Q5, Q6, Q7, Q8, Q9, Q10, Q11, Q12, Q13, Q14, Q15, Q16, Q17, Q18, Q19, Q20, Q21, Q22, Q23, Q24, Q25, Q26, Q27, Q28, Q29, Q30, Q31, Q32, Q33, Q34, Q35, Q36, Q37, Q38, Q39, Q40, Q41, Q42, Q43, Q44, Q45, Q46, Q47, Q48, Q49, Q50, Q51, Q52, Q53, Q54, Q55, Q56, Q57, Q58, Q59, Q60, Q61, Q62]), "oppositeDirection" : true, "depth" : 24 * mm});
        }
        {
            var Q0;
            Q0=sQuery(id+"F0.wireOp",VERTEX,"E32.center");
            var Q1;
            Q1=sQuery(id+"F0.wireOp",VERTEX,"E29.center");
            var Q2;
            Q2=sQuery(id+"F0.wireOp",VERTEX,"E38.center");
            var Q3;
            Q3=sQuery(id+"F0.wireOp",VERTEX,"E34.center");
            var Q4;
            Q4=makeQuery(id+"F1.opExtrude","SWEPT_BODY",BODY,{"disambiguationData":[OSD([sQuery(id+"F0.wireOp",EDGE,"E39"),sQuery(id+"F0.wireOp",EDGE,"E71")])]});
            hole(context, id + "F2", {"style" : HoleStyle.SIMPLE, "endStyle" : HoleEndStyle.BLIND, "holeDiameter" : 4 * mm, "holeDepth" : 8 * mm, "isTappedThrough" : true, "tappedDepth" : 12 * mm, "tapClearance" : 3, "locations" : qUnion([Q0, Q1, Q2, Q3]), "scope" : qUnion([Q4])});
        }
        {
            var Q0;
            Q0=sQuery(id+"F0.wireOp",VERTEX,"E73.center");
            var Q1;
            Q1=sQuery(id+"F0.wireOp",VERTEX,"E75.center");
            var Q2;
            Q2=sQuery(id+"F0.wireOp",VERTEX,"E76.center");
            var Q3;
            Q3=sQuery(id+"F0.wireOp",VERTEX,"E74.center");
            var Q4;
            Q4=makeQuery(id+"F1.opExtrude","SWEPT_BODY",BODY,{"disambiguationData":[OSD([sQuery(id+"F0.wireOp",EDGE,"E39"),sQuery(id+"F0.wireOp",EDGE,"E71")])]});
            hole(context, id + "F3", {"style" : HoleStyle.SIMPLE, "endStyle" : HoleEndStyle.THROUGH, "holeDiameter" : 7 * mm, "isTappedThrough" : true, "tappedDepth" : 12 * mm, "tapClearance" : 3, "locations" : qUnion([Q0, Q1, Q2, Q3]), "scope" : qUnion([Q4])});
        }
        {
            var Q0;
            {var subQ6=sQuery(id+"F0.wireOp",EDGE,"E64");var subQ11=sQuery(id+"F0.wireOp",EDGE,"E42");var subQ12=makeQuery(id+"F0.imprint","INTERSECT",VERTEX,{"disambiguationData":[OD(0.0)],"derivedFrom":[subQ11,subQ6]});Q0=makeQuery(id+"F0.imprint","IMPRINT",FACE,{"disambiguationData":[TD([[makeQuery(id+"F0.imprint","IMPRINT",EDGE,{"disambiguationData":[TD([[subQ12,1.0]])],"derivedFrom":subQ11}),-1.0]])]});}
            var Q1;
            {var subQ5=sQuery(id+"F0.wireOp",EDGE,"E63");var subQ11=sQuery(id+"F0.wireOp",EDGE,"E42");var subQ14=makeQuery(id+"F0.imprint","INTERSECT",VERTEX,{"disambiguationData":[OD(0.0)],"derivedFrom":[subQ11,subQ5]});Q1=makeQuery(id+"F0.imprint","IMPRINT",FACE,{"disambiguationData":[TD([[makeQuery(id+"F0.imprint","IMPRINT",EDGE,{"disambiguationData":[TD([[subQ14,1.0]])],"derivedFrom":subQ11}),-1.0]])]});}
            var Q2;
            {var subQ5=sQuery(id+"F0.wireOp",EDGE,"E63");var subQ11=sQuery(id+"F0.wireOp",EDGE,"E42");var subQ12=makeQuery(id+"F0.imprint","INTERSECT",VERTEX,{"disambiguationData":[OD(0.0)],"derivedFrom":[subQ11,subQ5]});Q2=makeQuery(id+"F0.imprint","IMPRINT",FACE,{"disambiguationData":[TD([[makeQuery(id+"F0.imprint","IMPRINT",EDGE,{"disambiguationData":[TD([[subQ12,-1.0]])],"derivedFrom":subQ11}),-1.0]])]});}
            var Q3;
            {var subQ5=sQuery(id+"F0.wireOp",EDGE,"E64");var subQ6=sQuery(id+"F0.wireOp",EDGE,"E42");var subQ7=makeQuery(id+"F0.imprint","INTERSECT",VERTEX,{"disambiguationData":[OD(1.0)],"derivedFrom":[subQ6,subQ5]});Q3=makeQuery(id+"F0.imprint","IMPRINT",FACE,{"disambiguationData":[TD([[makeQuery(id+"F0.imprint","IMPRINT",EDGE,{"disambiguationData":[TD([[subQ7,-1.0]])],"derivedFrom":subQ6}),-1.0]])]});}
            var Q4;
            {var subQ0=sQuery(id+"F0.wireOp",EDGE,"E64");var subQ1=sQuery(id+"F0.wireOp",EDGE,"E43");var subQ2=makeQuery(id+"F0.imprint","INTERSECT",VERTEX,{"disambiguationData":[OD(0.0)],"derivedFrom":[subQ1,subQ0]});Q4=makeQuery(id+"F0.imprint","IMPRINT",FACE,{"disambiguationData":[TD([[makeQuery(id+"F0.imprint","IMPRINT",EDGE,{"disambiguationData":[TD([[subQ2,1.0]])],"derivedFrom":subQ1}),-1.0]])]});}
            var Q5;
            {var subQ0=sQuery(id+"F0.wireOp",EDGE,"E63");var subQ1=sQuery(id+"F0.wireOp",EDGE,"E43");var subQ2=makeQuery(id+"F0.imprint","INTERSECT",VERTEX,{"disambiguationData":[OD(0.0)],"derivedFrom":[subQ1,subQ0]});Q5=makeQuery(id+"F0.imprint","IMPRINT",FACE,{"disambiguationData":[TD([[makeQuery(id+"F0.imprint","IMPRINT",EDGE,{"disambiguationData":[TD([[subQ2,1.0]])],"derivedFrom":subQ1}),-1.0]])]});}
            var Q6;
            {var subQ0=sQuery(id+"F0.wireOp",EDGE,"E63");var subQ1=sQuery(id+"F0.wireOp",EDGE,"E43");var subQ2=makeQuery(id+"F0.imprint","INTERSECT",VERTEX,{"disambiguationData":[OD(0.0)],"derivedFrom":[subQ1,subQ0]});Q6=makeQuery(id+"F0.imprint","IMPRINT",FACE,{"disambiguationData":[TD([[makeQuery(id+"F0.imprint","IMPRINT",EDGE,{"disambiguationData":[TD([[subQ2,-1.0]])],"derivedFrom":subQ1}),-1.0]])]});}
            var Q7;
            {var subQ0=sQuery(id+"F0.wireOp",EDGE,"E64");var subQ1=sQuery(id+"F0.wireOp",EDGE,"E43");var subQ2=makeQuery(id+"F0.imprint","INTERSECT",VERTEX,{"disambiguationData":[OD(1.0)],"derivedFrom":[subQ1,subQ0]});Q7=makeQuery(id+"F0.imprint","IMPRINT",FACE,{"disambiguationData":[TD([[makeQuery(id+"F0.imprint","IMPRINT",EDGE,{"disambiguationData":[TD([[subQ2,-1.0]])],"derivedFrom":subQ1}),-1.0]])]});}
            var Q8;
            {var subQ0=sQuery(id+"F0.wireOp",EDGE,"E47");var subQ1=sQuery(id+"F0.wireOp",EDGE,"E45");var subQ2=makeQuery(id+"F0.imprint","INTERSECT",VERTEX,{"disambiguationData":[OD(1.0)],"derivedFrom":[subQ1,subQ0]});Q8=makeQuery(id+"F0.imprint","IMPRINT",FACE,{"disambiguationData":[TD([[makeQuery(id+"F0.imprint","IMPRINT",EDGE,{"disambiguationData":[TD([[subQ2,1.0]])],"derivedFrom":subQ1}),1.0]])]});}
            var Q9;
            {var subQ0=sQuery(id+"F0.wireOp",EDGE,"E47");var subQ1=sQuery(id+"F0.wireOp",EDGE,"E45");var subQ2=makeQuery(id+"F0.imprint","INTERSECT",VERTEX,{"disambiguationData":[OD(0.0)],"derivedFrom":[subQ1,subQ0]});Q9=makeQuery(id+"F0.imprint","IMPRINT",FACE,{"disambiguationData":[TD([[makeQuery(id+"F0.imprint","IMPRINT",EDGE,{"disambiguationData":[TD([[subQ2,-1.0]])],"derivedFrom":subQ1}),1.0]])]});}
            var Q10;
            {var subQ0=sQuery(id+"F0.wireOp",EDGE,"E47");var subQ1=sQuery(id+"F0.wireOp",EDGE,"E45");var subQ2=makeQuery(id+"F0.imprint","INTERSECT",VERTEX,{"disambiguationData":[OD(0.0)],"derivedFrom":[subQ1,subQ0]});Q10=makeQuery(id+"F0.imprint","IMPRINT",FACE,{"disambiguationData":[TD([[makeQuery(id+"F0.imprint","IMPRINT",EDGE,{"disambiguationData":[TD([[subQ2,-1.0]])],"derivedFrom":subQ1}),-1.0]])]});}
            var Q11;
            {var subQ0=sQuery(id+"F0.wireOp",EDGE,"E48");var subQ1=sQuery(id+"F0.wireOp",EDGE,"E45");var subQ2=makeQuery(id+"F0.imprint","INTERSECT",VERTEX,{"derivedFrom":[subQ1,subQ0]});Q11=makeQuery(id+"F0.imprint","IMPRINT",FACE,{"disambiguationData":[TD([[makeQuery(id+"F0.imprint","IMPRINT",EDGE,{"disambiguationData":[TD([[subQ2,-1.0]])],"derivedFrom":subQ1}),-1.0]])]});}
            var Q12;
            {var subQ0=sQuery(id+"F0.wireOp",EDGE,"E48");var subQ1=sQuery(id+"F0.wireOp",EDGE,"E45");var subQ2=makeQuery(id+"F0.imprint","INTERSECT",VERTEX,{"derivedFrom":[subQ1,subQ0]});Q12=makeQuery(id+"F0.imprint","IMPRINT",FACE,{"disambiguationData":[TD([[makeQuery(id+"F0.imprint","IMPRINT",EDGE,{"disambiguationData":[TD([[subQ2,-1.0]])],"derivedFrom":subQ1}),1.0]])]});}
            var Q13;
            {var subQ0=sQuery(id+"F0.wireOp",EDGE,"E46");var subQ1=sQuery(id+"F0.wireOp",EDGE,"E45");var subQ2=makeQuery(id+"F0.imprint","INTERSECT",VERTEX,{"disambiguationData":[OD(0.0)],"derivedFrom":[subQ1,subQ0]});Q13=makeQuery(id+"F0.imprint","IMPRINT",FACE,{"disambiguationData":[TD([[makeQuery(id+"F0.imprint","IMPRINT",EDGE,{"disambiguationData":[TD([[subQ2,-1.0]])],"derivedFrom":subQ1}),1.0]])]});}
            var Q14;
            {var subQ0=sQuery(id+"F0.wireOp",EDGE,"E47");var subQ1=sQuery(id+"F0.wireOp",EDGE,"E45");var subQ2=makeQuery(id+"F0.imprint","INTERSECT",VERTEX,{"disambiguationData":[OD(1.0)],"derivedFrom":[subQ1,subQ0]});Q14=makeQuery(id+"F0.imprint","IMPRINT",FACE,{"disambiguationData":[TD([[makeQuery(id+"F0.imprint","IMPRINT",EDGE,{"disambiguationData":[TD([[subQ2,1.0]])],"derivedFrom":subQ1}),-1.0]])]});}
            var Q15;
            {var subQ0=sQuery(id+"F0.wireOp",EDGE,"E46");var subQ1=sQuery(id+"F0.wireOp",EDGE,"E45");var subQ2=makeQuery(id+"F0.imprint","INTERSECT",VERTEX,{"disambiguationData":[OD(0.0)],"derivedFrom":[subQ1,subQ0]});Q15=makeQuery(id+"F0.imprint","IMPRINT",FACE,{"disambiguationData":[TD([[makeQuery(id+"F0.imprint","IMPRINT",EDGE,{"disambiguationData":[TD([[subQ2,-1.0]])],"derivedFrom":subQ1}),-1.0]])]});}
            var Q16;
            {var subQ0=sQuery(id+"F0.wireOp",EDGE,"E52");var subQ1=sQuery(id+"F0.wireOp",EDGE,"E49");var subQ2=makeQuery(id+"F0.imprint","INTERSECT",VERTEX,{"derivedFrom":[subQ1,subQ0]});Q16=makeQuery(id+"F0.imprint","IMPRINT",FACE,{"disambiguationData":[TD([[makeQuery(id+"F0.imprint","IMPRINT",EDGE,{"disambiguationData":[TD([[subQ2,-1.0]])],"derivedFrom":subQ1}),-1.0]])]});}
            var Q17;
            {var subQ0=sQuery(id+"F0.wireOp",EDGE,"E52");var subQ1=sQuery(id+"F0.wireOp",EDGE,"E49");var subQ2=makeQuery(id+"F0.imprint","INTERSECT",VERTEX,{"derivedFrom":[subQ1,subQ0]});Q17=makeQuery(id+"F0.imprint","IMPRINT",FACE,{"disambiguationData":[TD([[makeQuery(id+"F0.imprint","IMPRINT",EDGE,{"disambiguationData":[TD([[subQ2,-1.0]])],"derivedFrom":subQ1}),1.0]])]});}
            var Q18;
            {var subQ0=sQuery(id+"F0.wireOp",EDGE,"E50");var subQ1=sQuery(id+"F0.wireOp",EDGE,"E49");var subQ2=makeQuery(id+"F0.imprint","INTERSECT",VERTEX,{"disambiguationData":[OD(0.0)],"derivedFrom":[subQ1,subQ0]});Q18=makeQuery(id+"F0.imprint","IMPRINT",FACE,{"disambiguationData":[TD([[makeQuery(id+"F0.imprint","IMPRINT",EDGE,{"disambiguationData":[TD([[subQ2,-1.0]])],"derivedFrom":subQ1}),1.0]])]});}
            var Q19;
            {var subQ0=sQuery(id+"F0.wireOp",EDGE,"E50");var subQ1=sQuery(id+"F0.wireOp",EDGE,"E49");var subQ2=makeQuery(id+"F0.imprint","INTERSECT",VERTEX,{"disambiguationData":[OD(0.0)],"derivedFrom":[subQ1,subQ0]});Q19=makeQuery(id+"F0.imprint","IMPRINT",FACE,{"disambiguationData":[TD([[makeQuery(id+"F0.imprint","IMPRINT",EDGE,{"disambiguationData":[TD([[subQ2,-1.0]])],"derivedFrom":subQ1}),-1.0]])]});}
            var Q20;
            {var subQ0=sQuery(id+"F0.wireOp",EDGE,"E51");var subQ1=sQuery(id+"F0.wireOp",EDGE,"E49");var subQ2=makeQuery(id+"F0.imprint","INTERSECT",VERTEX,{"disambiguationData":[OD(1.0)],"derivedFrom":[subQ1,subQ0]});Q20=makeQuery(id+"F0.imprint","IMPRINT",FACE,{"disambiguationData":[TD([[makeQuery(id+"F0.imprint","IMPRINT",EDGE,{"disambiguationData":[TD([[subQ2,1.0]])],"derivedFrom":subQ1}),-1.0]])]});}
            var Q21;
            {var subQ0=sQuery(id+"F0.wireOp",EDGE,"E51");var subQ1=sQuery(id+"F0.wireOp",EDGE,"E49");var subQ2=makeQuery(id+"F0.imprint","INTERSECT",VERTEX,{"disambiguationData":[OD(1.0)],"derivedFrom":[subQ1,subQ0]});Q21=makeQuery(id+"F0.imprint","IMPRINT",FACE,{"disambiguationData":[TD([[makeQuery(id+"F0.imprint","IMPRINT",EDGE,{"disambiguationData":[TD([[subQ2,1.0]])],"derivedFrom":subQ1}),1.0]])]});}
            var Q22;
            {var subQ0=sQuery(id+"F0.wireOp",EDGE,"E51");var subQ1=sQuery(id+"F0.wireOp",EDGE,"E49");var subQ2=makeQuery(id+"F0.imprint","INTERSECT",VERTEX,{"disambiguationData":[OD(0.0)],"derivedFrom":[subQ1,subQ0]});Q22=makeQuery(id+"F0.imprint","IMPRINT",FACE,{"disambiguationData":[TD([[makeQuery(id+"F0.imprint","IMPRINT",EDGE,{"disambiguationData":[TD([[subQ2,-1.0]])],"derivedFrom":subQ1}),-1.0]])]});}
            var Q23;
            {var subQ0=sQuery(id+"F0.wireOp",EDGE,"E51");var subQ1=sQuery(id+"F0.wireOp",EDGE,"E49");var subQ2=makeQuery(id+"F0.imprint","INTERSECT",VERTEX,{"disambiguationData":[OD(0.0)],"derivedFrom":[subQ1,subQ0]});Q23=makeQuery(id+"F0.imprint","IMPRINT",FACE,{"disambiguationData":[TD([[makeQuery(id+"F0.imprint","IMPRINT",EDGE,{"disambiguationData":[TD([[subQ2,-1.0]])],"derivedFrom":subQ1}),1.0]])]});}
            var Q24;
            {var subQ0=sQuery(id+"F0.wireOp",EDGE,"E56");var subQ1=sQuery(id+"F0.wireOp",EDGE,"E53");var subQ2=makeQuery(id+"F0.imprint","INTERSECT",VERTEX,{"derivedFrom":[subQ1,subQ0]});Q24=makeQuery(id+"F0.imprint","IMPRINT",FACE,{"disambiguationData":[TD([[makeQuery(id+"F0.imprint","IMPRINT",EDGE,{"disambiguationData":[TD([[subQ2,-1.0]])],"derivedFrom":subQ1}),-1.0]])]});}
            var Q25;
            {var subQ0=sQuery(id+"F0.wireOp",EDGE,"E56");var subQ1=sQuery(id+"F0.wireOp",EDGE,"E53");var subQ2=makeQuery(id+"F0.imprint","INTERSECT",VERTEX,{"derivedFrom":[subQ1,subQ0]});Q25=makeQuery(id+"F0.imprint","IMPRINT",FACE,{"disambiguationData":[TD([[makeQuery(id+"F0.imprint","IMPRINT",EDGE,{"disambiguationData":[TD([[subQ2,-1.0]])],"derivedFrom":subQ1}),1.0]])]});}
            var Q26;
            {var subQ0=sQuery(id+"F0.wireOp",EDGE,"E54");var subQ1=sQuery(id+"F0.wireOp",EDGE,"E53");var subQ2=makeQuery(id+"F0.imprint","INTERSECT",VERTEX,{"disambiguationData":[OD(0.0)],"derivedFrom":[subQ1,subQ0]});Q26=makeQuery(id+"F0.imprint","IMPRINT",FACE,{"disambiguationData":[TD([[makeQuery(id+"F0.imprint","IMPRINT",EDGE,{"disambiguationData":[TD([[subQ2,-1.0]])],"derivedFrom":subQ1}),1.0]])]});}
            var Q27;
            {var subQ0=sQuery(id+"F0.wireOp",EDGE,"E54");var subQ1=sQuery(id+"F0.wireOp",EDGE,"E53");var subQ2=makeQuery(id+"F0.imprint","INTERSECT",VERTEX,{"disambiguationData":[OD(0.0)],"derivedFrom":[subQ1,subQ0]});Q27=makeQuery(id+"F0.imprint","IMPRINT",FACE,{"disambiguationData":[TD([[makeQuery(id+"F0.imprint","IMPRINT",EDGE,{"disambiguationData":[TD([[subQ2,-1.0]])],"derivedFrom":subQ1}),-1.0]])]});}
            var Q28;
            {var subQ0=sQuery(id+"F0.wireOp",EDGE,"E55");var subQ1=sQuery(id+"F0.wireOp",EDGE,"E53");var subQ2=makeQuery(id+"F0.imprint","INTERSECT",VERTEX,{"disambiguationData":[OD(1.0)],"derivedFrom":[subQ1,subQ0]});Q28=makeQuery(id+"F0.imprint","IMPRINT",FACE,{"disambiguationData":[TD([[makeQuery(id+"F0.imprint","IMPRINT",EDGE,{"disambiguationData":[TD([[subQ2,1.0]])],"derivedFrom":subQ1}),-1.0]])]});}
            var Q29;
            {var subQ0=sQuery(id+"F0.wireOp",EDGE,"E55");var subQ1=sQuery(id+"F0.wireOp",EDGE,"E53");var subQ2=makeQuery(id+"F0.imprint","INTERSECT",VERTEX,{"disambiguationData":[OD(1.0)],"derivedFrom":[subQ1,subQ0]});Q29=makeQuery(id+"F0.imprint","IMPRINT",FACE,{"disambiguationData":[TD([[makeQuery(id+"F0.imprint","IMPRINT",EDGE,{"disambiguationData":[TD([[subQ2,1.0]])],"derivedFrom":subQ1}),1.0]])]});}
            var Q30;
            {var subQ0=sQuery(id+"F0.wireOp",EDGE,"E55");var subQ1=sQuery(id+"F0.wireOp",EDGE,"E53");var subQ2=makeQuery(id+"F0.imprint","INTERSECT",VERTEX,{"disambiguationData":[OD(0.0)],"derivedFrom":[subQ1,subQ0]});Q30=makeQuery(id+"F0.imprint","IMPRINT",FACE,{"disambiguationData":[TD([[makeQuery(id+"F0.imprint","IMPRINT",EDGE,{"disambiguationData":[TD([[subQ2,-1.0]])],"derivedFrom":subQ1}),1.0]])]});}
            var Q31;
            {var subQ0=sQuery(id+"F0.wireOp",EDGE,"E55");var subQ1=sQuery(id+"F0.wireOp",EDGE,"E53");var subQ2=makeQuery(id+"F0.imprint","INTERSECT",VERTEX,{"disambiguationData":[OD(0.0)],"derivedFrom":[subQ1,subQ0]});Q31=makeQuery(id+"F0.imprint","IMPRINT",FACE,{"disambiguationData":[TD([[makeQuery(id+"F0.imprint","IMPRINT",EDGE,{"disambiguationData":[TD([[subQ2,-1.0]])],"derivedFrom":subQ1}),-1.0]])]});}
            var Q32;
            {var subQ0=sQuery(id+"F0.wireOp",EDGE,"E58");var subQ1=sQuery(id+"F0.wireOp",EDGE,"E57");var subQ2=makeQuery(id+"F0.imprint","INTERSECT",VERTEX,{"disambiguationData":[OD(0.0)],"derivedFrom":[subQ1,subQ0]});Q32=makeQuery(id+"F0.imprint","IMPRINT",FACE,{"disambiguationData":[TD([[makeQuery(id+"F0.imprint","IMPRINT",EDGE,{"disambiguationData":[TD([[subQ2,-1.0]])],"derivedFrom":subQ1}),1.0]])]});}
            var Q33;
            {var subQ0=sQuery(id+"F0.wireOp",EDGE,"E58");var subQ1=sQuery(id+"F0.wireOp",EDGE,"E57");var subQ2=makeQuery(id+"F0.imprint","INTERSECT",VERTEX,{"disambiguationData":[OD(0.0)],"derivedFrom":[subQ1,subQ0]});Q33=makeQuery(id+"F0.imprint","IMPRINT",FACE,{"disambiguationData":[TD([[makeQuery(id+"F0.imprint","IMPRINT",EDGE,{"disambiguationData":[TD([[subQ2,-1.0]])],"derivedFrom":subQ1}),-1.0]])]});}
            var Q34;
            {var subQ0=sQuery(id+"F0.wireOp",EDGE,"E59");var subQ1=sQuery(id+"F0.wireOp",EDGE,"E57");var subQ2=makeQuery(id+"F0.imprint","INTERSECT",VERTEX,{"disambiguationData":[OD(1.0)],"derivedFrom":[subQ1,subQ0]});Q34=makeQuery(id+"F0.imprint","IMPRINT",FACE,{"disambiguationData":[TD([[makeQuery(id+"F0.imprint","IMPRINT",EDGE,{"disambiguationData":[TD([[subQ2,1.0]])],"derivedFrom":subQ1}),-1.0]])]});}
            var Q35;
            {var subQ0=sQuery(id+"F0.wireOp",EDGE,"E59");var subQ1=sQuery(id+"F0.wireOp",EDGE,"E57");var subQ2=makeQuery(id+"F0.imprint","INTERSECT",VERTEX,{"disambiguationData":[OD(1.0)],"derivedFrom":[subQ1,subQ0]});Q35=makeQuery(id+"F0.imprint","IMPRINT",FACE,{"disambiguationData":[TD([[makeQuery(id+"F0.imprint","IMPRINT",EDGE,{"disambiguationData":[TD([[subQ2,1.0]])],"derivedFrom":subQ1}),1.0]])]});}
            var Q36;
            {var subQ0=sQuery(id+"F0.wireOp",EDGE,"E59");var subQ1=sQuery(id+"F0.wireOp",EDGE,"E57");var subQ2=makeQuery(id+"F0.imprint","INTERSECT",VERTEX,{"disambiguationData":[OD(0.0)],"derivedFrom":[subQ1,subQ0]});Q36=makeQuery(id+"F0.imprint","IMPRINT",FACE,{"disambiguationData":[TD([[makeQuery(id+"F0.imprint","IMPRINT",EDGE,{"disambiguationData":[TD([[subQ2,-1.0]])],"derivedFrom":subQ1}),1.0]])]});}
            var Q37;
            {var subQ0=sQuery(id+"F0.wireOp",EDGE,"E59");var subQ1=sQuery(id+"F0.wireOp",EDGE,"E57");var subQ2=makeQuery(id+"F0.imprint","INTERSECT",VERTEX,{"disambiguationData":[OD(0.0)],"derivedFrom":[subQ1,subQ0]});Q37=makeQuery(id+"F0.imprint","IMPRINT",FACE,{"disambiguationData":[TD([[makeQuery(id+"F0.imprint","IMPRINT",EDGE,{"disambiguationData":[TD([[subQ2,-1.0]])],"derivedFrom":subQ1}),-1.0]])]});}
            var Q38;
            {var subQ0=sQuery(id+"F0.wireOp",EDGE,"E60");var subQ1=sQuery(id+"F0.wireOp",EDGE,"E57");var subQ2=makeQuery(id+"F0.imprint","INTERSECT",VERTEX,{"derivedFrom":[subQ1,subQ0]});Q38=makeQuery(id+"F0.imprint","IMPRINT",FACE,{"disambiguationData":[TD([[makeQuery(id+"F0.imprint","IMPRINT",EDGE,{"disambiguationData":[TD([[subQ2,-1.0]])],"derivedFrom":subQ1}),-1.0]])]});}
            var Q39;
            {var subQ0=sQuery(id+"F0.wireOp",EDGE,"E60");var subQ1=sQuery(id+"F0.wireOp",EDGE,"E57");var subQ2=makeQuery(id+"F0.imprint","INTERSECT",VERTEX,{"derivedFrom":[subQ1,subQ0]});Q39=makeQuery(id+"F0.imprint","IMPRINT",FACE,{"disambiguationData":[TD([[makeQuery(id+"F0.imprint","IMPRINT",EDGE,{"disambiguationData":[TD([[subQ2,-1.0]])],"derivedFrom":subQ1}),1.0]])]});}
            extrude(context, id + "F4", {"entities" : qUnion([Q0, Q1, Q2, Q3, Q4, Q5, Q6, Q7, Q8, Q9, Q10, Q11, Q12, Q13, Q14, Q15, Q16, Q17, Q18, Q19, Q20, Q21, Q22, Q23, Q24, Q25, Q26, Q27, Q28, Q29, Q30, Q31, Q32, Q33, Q34, Q35, Q36, Q37, Q38, Q39]), "oppositeDirection" : true, "depth" : 58 * mm});
        }
        {
            var Q0;
            Q0=sQuery(id+"F0.wireOp",VERTEX,"E47.center");
            var Q1;
            Q1=sQuery(id+"F0.wireOp",VERTEX,"E55.center");
            var Q2;
            Q2=sQuery(id+"F0.wireOp",VERTEX,"E51.center");
            var Q3;
            Q3=sQuery(id+"F0.wireOp",VERTEX,"E59.center");
            var Q4;
            Q4=makeQuery(id+"F4.opExtrude","SWEPT_BODY",BODY,{"disambiguationData":[OSD([sQuery(id+"F0.wireOp",EDGE,"E42")])]});
            hole(context, id + "F5", {"style" : HoleStyle.SIMPLE, "endStyle" : HoleEndStyle.BLIND, "holeDiameter" : 5 * mm, "holeDepth" : 10 * mm, "isTappedThrough" : true, "tappedDepth" : 12 * mm, "tapClearance" : 3, "locations" : qUnion([Q0, Q1, Q2, Q3]), "scope" : qUnion([Q4])});
        }
        {
            var Q0;
            Q0=sQuery(id+"F0.wireOp",VERTEX,"E43.center");
            var Q1;
            Q1=makeQuery(id+"F4.opExtrude","SWEPT_BODY",BODY,{"disambiguationData":[OSD([sQuery(id+"F0.wireOp",EDGE,"E42")])]});
            hole(context, id + "F6", {"style" : HoleStyle.SIMPLE, "endStyle" : HoleEndStyle.THROUGH, "holeDiameter" : 26 * mm, "isTappedThrough" : true, "tappedDepth" : 12 * mm, "tapClearance" : 3, "locations" : qUnion([Q0]), "scope" : qUnion([Q1])});
        }
        {
            var Q0;
            Q0=makeQuery(id+"F4.opExtrude","CAP_FACE",FACE,{"disambiguationData":[OSD([sQuery(id+"F0.wireOp",EDGE,"E42")])],"isStart":false});
            var sketch = newSketch(context, id + "F7", { "sketchPlane" : qUnion([Q0])});
            skPoint(sketch, "E123", {"position": v(176.66, 2.45) * mm});
            skSolve(sketch);
        }
        {
            var Q0;
            Q0=sQuery(id+"F7.wireOp",VERTEX,"E123");
            var Q1;
            Q1=makeQuery(id+"F4.opExtrude","SWEPT_BODY",BODY,{"disambiguationData":[OSD([sQuery(id+"F0.wireOp",EDGE,"E42")])]});
            hole(context, id + "F8", {"style" : HoleStyle.SIMPLE, "endStyle" : HoleEndStyle.BLIND, "holeDiameter" : 28 * mm, "holeDepth" : 9 * mm, "isTappedThrough" : true, "tappedDepth" : 12 * mm, "tapClearance" : 3, "locations" : qUnion([Q0]), "scope" : qUnion([Q1])});
        }
        {
            var Q0;
            Q0=makeQuery(id+"F1.opExtrude","CAP_EDGE",EDGE,{"disambiguationData":[OSD([sQuery(id+"F0.wireOp",EDGE,"E39")])],"isStart":true});
            chamfer(context, id + "F9", {"entities" : qUnion([Q0]), "width" : 1 * mm, "tangentPropagation" : true});
        }
        {
            var Q0;
            Q0=makeQuery(id+"F1.opExtrude","CAP_EDGE",EDGE,{"disambiguationData":[OSD([sQuery(id+"F0.wireOp",EDGE,"E71")])],"isStart":true});
            var Q1;
            Q1=makeQuery(id+"F1.opExtrude","CAP_EDGE",EDGE,{"disambiguationData":[OSD([sQuery(id+"F0.wireOp",EDGE,"E71")])],"isStart":false});
            chamfer(context, id + "F10", {"entities" : qUnion([Q0, Q1]), "width" : 1 * mm, "tangentPropagation" : true});
        }
    });
